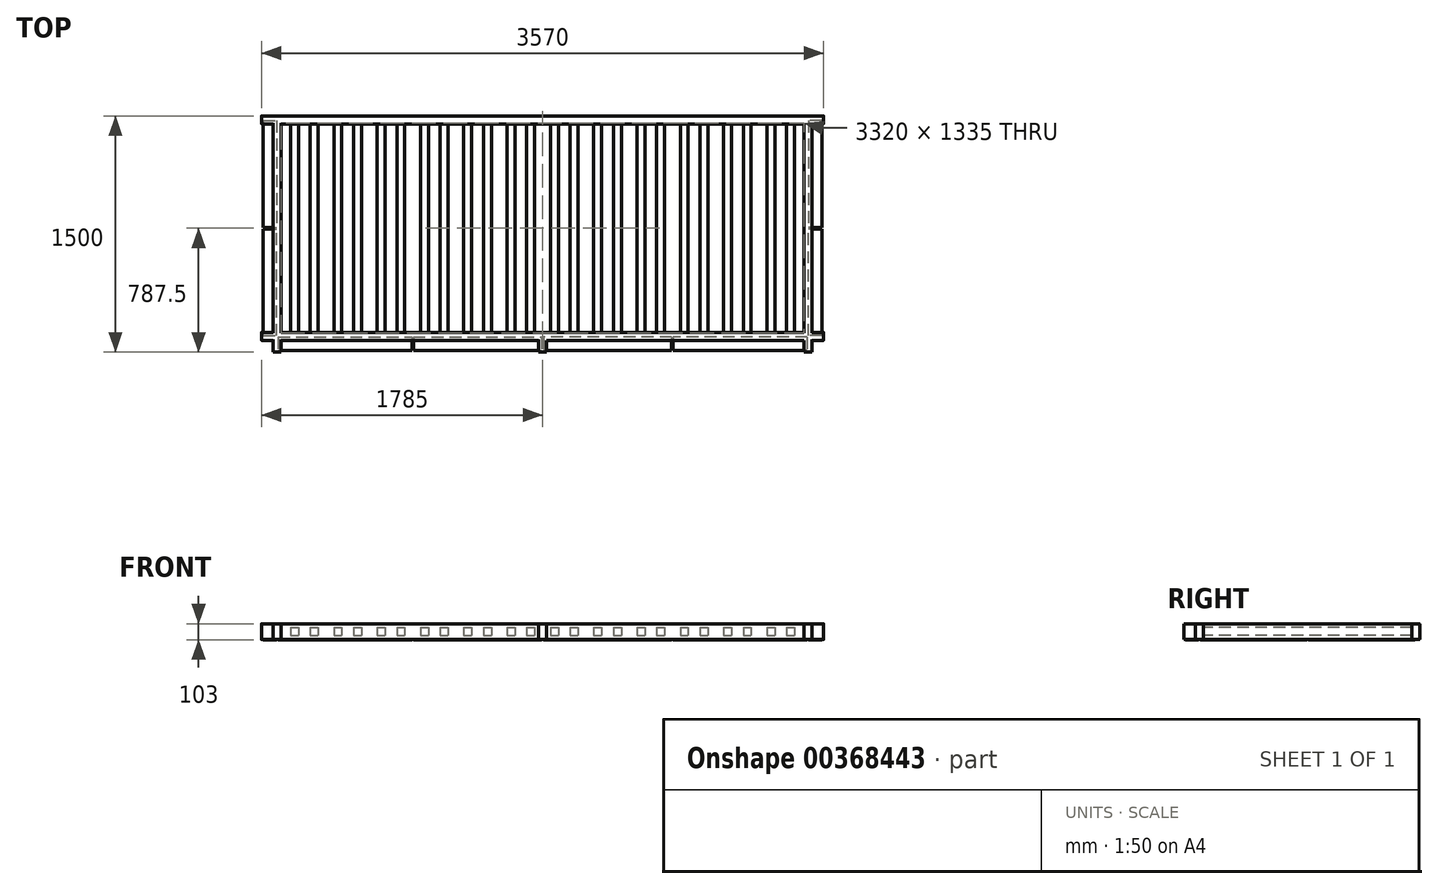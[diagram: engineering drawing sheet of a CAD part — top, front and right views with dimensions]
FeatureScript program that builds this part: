
annotation { "Feature Type Name" : "Feature", "Feature Type Description" : "" }
export const myFeature = defineFeature(function(context is Context, id is Id, definition is map)
    precondition{}
    {
        {
            var Q0;
            Q0=qCreatedBy(makeId("Top.planeOp"),FACE);
            var sketch = newSketch(context, id + "F0", { "sketchPlane" : qUnion([Q0])});
            skLineSegment(sketch, "E0.bottom", {"start": v(0, 0) * mm, "end": v(3570, 0) * mm, "construction": true});
            skLineSegment(sketch, "E0.top", {"start": v(0, 1500) * mm, "end": v(3570, 1500) * mm, "construction": true});
            skLineSegment(sketch, "E0.left", {"start": v(0, 0) * mm, "end": v(0, 1500) * mm, "construction": true});
            skLineSegment(sketch, "E0.right", {"start": v(3570, 0) * mm, "end": v(3570, 1500) * mm, "construction": true});
            skLineSegment(sketch, "E1.bottom", {"start": v(0, 1500) * mm, "end": v(3570, 1500) * mm});
            skLineSegment(sketch, "E1.top", {"start": v(0, 1450) * mm, "end": v(3570, 1450) * mm});
            skLineSegment(sketch, "E1.left", {"start": v(0, 1500) * mm, "end": v(0, 1450) * mm});
            skLineSegment(sketch, "E1.right", {"start": v(3570, 1500) * mm, "end": v(3570, 1450) * mm});
            skLineSegment(sketch, "E2.bottom", {"start": v(0, 125) * mm, "end": v(3570, 125) * mm});
            skLineSegment(sketch, "E2.top", {"start": v(0, 75) * mm, "end": v(3570, 75) * mm});
            skLineSegment(sketch, "E2.left", {"start": v(0, 125) * mm, "end": v(0, 75) * mm});
            skLineSegment(sketch, "E2.right", {"start": v(3570, 125) * mm, "end": v(3570, 75) * mm});
            skLineSegment(sketch, "E3.bottom", {"start": v(75, 1500) * mm, "end": v(125, 1500) * mm});
            skLineSegment(sketch, "E3.top", {"start": v(75, 0) * mm, "end": v(125, 0) * mm});
            skLineSegment(sketch, "E3.left", {"start": v(75, 1500) * mm, "end": v(75, 0) * mm});
            skLineSegment(sketch, "E3.right", {"start": v(125, 1500) * mm, "end": v(125, 0) * mm});
            skLineSegment(sketch, "E4.bottom", {"start": v(3445, 1500) * mm, "end": v(3495, 1500) * mm});
            skLineSegment(sketch, "E4.top", {"start": v(3445, 0) * mm, "end": v(3495, 0) * mm});
            skLineSegment(sketch, "E4.left", {"start": v(3445, 1500) * mm, "end": v(3445, 0) * mm});
            skLineSegment(sketch, "E4.right", {"start": v(3495, 1500) * mm, "end": v(3495, 0) * mm});
            skLineSegment(sketch, "E5.bottom", {"start": v(1810, 0) * mm, "end": v(1760, 0) * mm});
            skLineSegment(sketch, "E5.left", {"start": v(1810, 0) * mm, "end": v(1810, 75) * mm});
            skLineSegment(sketch, "E5.right", {"start": v(1760, 0) * mm, "end": v(1760, 75) * mm});
            skLineSegment(sketch, "E6", {"start": v(3495, 1450) * mm, "end": v(3495, 125) * mm, "construction": true});
            skLineSegment(sketch, "E7", {"start": v(75, 1450) * mm, "end": v(75, 125) * mm, "construction": true});
            skSolve(sketch);
        }
        {
            var Q0;
            Q0=qSketchRegion(id+"F0",true);
            extrude(context, id + "F1", {"entities" : qUnion([Q0]), "depth" : 75 * mm, "hasSecondDirection" : true, "secondDirectionOppositeDirection" : true, "secondDirectionDepth" : 25 * mm});
        }
        {
            var Q0;
            {var subQ0=sQuery(id+"F0.wireOp",EDGE,"E1.top");Q0=makeQuery(id+"F1.opExtrude","CAP_EDGE",EDGE,{"disambiguationData":[OSD([subQ0]),TDD([makeQuery(id+"F0.imprint","IMPRINT",EDGE,{"disambiguationData":[TD([[makeQuery(id+"F0.imprint","INTERSECT",VERTEX,{"derivedFrom":[subQ0,sQuery(id+"F0.wireOp",EDGE,"E3.right")]}),-1.0]])],"derivedFrom":subQ0})])],"isStart":false});}
            var Q1;
            Q1=makeQuery(id+"F1.opExtrude","CAP_EDGE",EDGE,{"disambiguationData":[OSD([sQuery(id+"F0.wireOp",EDGE,"E1.bottom"),sQuery(id+"F0.wireOp",EDGE,"E3.bottom"),sQuery(id+"F0.wireOp",EDGE,"E4.bottom")])],"isStart":false});
            var Q2;
            {var subQ0=sQuery(id+"F0.wireOp",EDGE,"E2.bottom");Q2=makeQuery(id+"F1.opExtrude","CAP_EDGE",EDGE,{"disambiguationData":[OSD([subQ0]),TDD([makeQuery(id+"F0.imprint","IMPRINT",EDGE,{"disambiguationData":[TD([[makeQuery(id+"F0.imprint","INTERSECT",VERTEX,{"derivedFrom":[subQ0,sQuery(id+"F0.wireOp",EDGE,"E3.right")]}),-1.0]])],"derivedFrom":subQ0})])],"isStart":false});}
            var Q3;
            {var subQ0=sQuery(id+"F0.wireOp",EDGE,"E2.top");Q3=makeQuery(id+"F1.opExtrude","CAP_EDGE",EDGE,{"disambiguationData":[OSD([subQ0]),TDD([makeQuery(id+"F0.imprint","IMPRINT",EDGE,{"disambiguationData":[TD([[makeQuery(id+"F0.imprint","INTERSECT",VERTEX,{"derivedFrom":[subQ0,sQuery(id+"F0.wireOp",EDGE,"E3.right")]}),-1.0]])],"derivedFrom":subQ0})])],"isStart":false});}
            var Q4;
            {var subQ0=sQuery(id+"F0.wireOp",EDGE,"E2.top");Q4=makeQuery(id+"F1.opExtrude","CAP_EDGE",EDGE,{"disambiguationData":[OSD([subQ0]),TDD([makeQuery(id+"F0.imprint","IMPRINT",EDGE,{"disambiguationData":[TD([[makeQuery(id+"F0.imprint","INTERSECT",VERTEX,{"derivedFrom":[subQ0,sQuery(id+"F0.wireOp",EDGE,"E2.left")]}),-1.0]])],"derivedFrom":subQ0})])],"isStart":false});}
            var Q5;
            {var subQ0=sQuery(id+"F0.wireOp",EDGE,"E2.bottom");Q5=makeQuery(id+"F1.opExtrude","CAP_EDGE",EDGE,{"disambiguationData":[OSD([subQ0]),TDD([makeQuery(id+"F0.imprint","IMPRINT",EDGE,{"disambiguationData":[TD([[makeQuery(id+"F0.imprint","INTERSECT",VERTEX,{"derivedFrom":[subQ0,sQuery(id+"F0.wireOp",EDGE,"E2.left")]}),-1.0]])],"derivedFrom":subQ0})])],"isStart":false});}
            var Q6;
            {var subQ0=sQuery(id+"F0.wireOp",EDGE,"E2.bottom");Q6=makeQuery(id+"F1.opExtrude","CAP_EDGE",EDGE,{"disambiguationData":[OSD([subQ0]),TDD([makeQuery(id+"F0.imprint","IMPRINT",EDGE,{"disambiguationData":[TD([[makeQuery(id+"F0.imprint","INTERSECT",VERTEX,{"derivedFrom":[subQ0,sQuery(id+"F0.wireOp",EDGE,"E2.right")]}),1.0]])],"derivedFrom":subQ0})])],"isStart":false});}
            var Q7;
            {var subQ0=sQuery(id+"F0.wireOp",EDGE,"E2.top");Q7=makeQuery(id+"F1.opExtrude","CAP_EDGE",EDGE,{"disambiguationData":[OSD([subQ0]),TDD([makeQuery(id+"F0.imprint","IMPRINT",EDGE,{"disambiguationData":[TD([[makeQuery(id+"F0.imprint","INTERSECT",VERTEX,{"derivedFrom":[subQ0,sQuery(id+"F0.wireOp",EDGE,"E2.right")]}),1.0]])],"derivedFrom":subQ0})])],"isStart":false});}
            var Q8;
            {var subQ0=sQuery(id+"F0.wireOp",EDGE,"E1.top");Q8=makeQuery(id+"F1.opExtrude","CAP_EDGE",EDGE,{"disambiguationData":[OSD([subQ0]),TDD([makeQuery(id+"F0.imprint","IMPRINT",EDGE,{"disambiguationData":[TD([[makeQuery(id+"F0.imprint","INTERSECT",VERTEX,{"derivedFrom":[subQ0,sQuery(id+"F0.wireOp",EDGE,"E1.right")]}),1.0]])],"derivedFrom":subQ0})])],"isStart":false});}
            var Q9;
            {var subQ0=sQuery(id+"F0.wireOp",EDGE,"E1.top");Q9=makeQuery(id+"F1.opExtrude","CAP_EDGE",EDGE,{"disambiguationData":[OSD([subQ0]),TDD([makeQuery(id+"F0.imprint","IMPRINT",EDGE,{"disambiguationData":[TD([[makeQuery(id+"F0.imprint","INTERSECT",VERTEX,{"derivedFrom":[subQ0,sQuery(id+"F0.wireOp",EDGE,"E1.left")]}),-1.0]])],"derivedFrom":subQ0})])],"isStart":false});}
            var Q10;
            Q10=makeQuery(id+"F1.opExtrude","CAP_EDGE",EDGE,{"disambiguationData":[OSD([sQuery(id+"F0.wireOp",EDGE,"E1.bottom"),sQuery(id+"F0.wireOp",EDGE,"E3.bottom"),sQuery(id+"F0.wireOp",EDGE,"E4.bottom")])],"isStart":true});
            var Q11;
            {var subQ0=sQuery(id+"F0.wireOp",EDGE,"E1.top");Q11=makeQuery(id+"F1.opExtrude","CAP_EDGE",EDGE,{"disambiguationData":[OSD([subQ0]),TDD([makeQuery(id+"F0.imprint","IMPRINT",EDGE,{"disambiguationData":[TD([[makeQuery(id+"F0.imprint","INTERSECT",VERTEX,{"derivedFrom":[subQ0,sQuery(id+"F0.wireOp",EDGE,"E3.right")]}),-1.0]])],"derivedFrom":subQ0})])],"isStart":true});}
            var Q12;
            {var subQ0=sQuery(id+"F0.wireOp",EDGE,"E1.top");Q12=makeQuery(id+"F1.opExtrude","CAP_EDGE",EDGE,{"disambiguationData":[OSD([subQ0]),TDD([makeQuery(id+"F0.imprint","IMPRINT",EDGE,{"disambiguationData":[TD([[makeQuery(id+"F0.imprint","INTERSECT",VERTEX,{"derivedFrom":[subQ0,sQuery(id+"F0.wireOp",EDGE,"E1.right")]}),1.0]])],"derivedFrom":subQ0})])],"isStart":true});}
            var Q13;
            {var subQ0=sQuery(id+"F0.wireOp",EDGE,"E2.top");Q13=makeQuery(id+"F1.opExtrude","CAP_EDGE",EDGE,{"disambiguationData":[OSD([subQ0]),TDD([makeQuery(id+"F0.imprint","IMPRINT",EDGE,{"disambiguationData":[TD([[makeQuery(id+"F0.imprint","INTERSECT",VERTEX,{"derivedFrom":[subQ0,sQuery(id+"F0.wireOp",EDGE,"E2.right")]}),1.0]])],"derivedFrom":subQ0})])],"isStart":true});}
            var Q14;
            {var subQ0=sQuery(id+"F0.wireOp",EDGE,"E2.bottom");Q14=makeQuery(id+"F1.opExtrude","CAP_EDGE",EDGE,{"disambiguationData":[OSD([subQ0]),TDD([makeQuery(id+"F0.imprint","IMPRINT",EDGE,{"disambiguationData":[TD([[makeQuery(id+"F0.imprint","INTERSECT",VERTEX,{"derivedFrom":[subQ0,sQuery(id+"F0.wireOp",EDGE,"E2.right")]}),1.0]])],"derivedFrom":subQ0})])],"isStart":true});}
            var Q15;
            {var subQ0=sQuery(id+"F0.wireOp",EDGE,"E2.bottom");Q15=makeQuery(id+"F1.opExtrude","CAP_EDGE",EDGE,{"disambiguationData":[OSD([subQ0]),TDD([makeQuery(id+"F0.imprint","IMPRINT",EDGE,{"disambiguationData":[TD([[makeQuery(id+"F0.imprint","INTERSECT",VERTEX,{"derivedFrom":[subQ0,sQuery(id+"F0.wireOp",EDGE,"E3.right")]}),-1.0]])],"derivedFrom":subQ0})])],"isStart":true});}
            var Q16;
            {var subQ0=sQuery(id+"F0.wireOp",EDGE,"E2.top");Q16=makeQuery(id+"F1.opExtrude","CAP_EDGE",EDGE,{"disambiguationData":[OSD([subQ0]),TDD([makeQuery(id+"F0.imprint","IMPRINT",EDGE,{"disambiguationData":[TD([[makeQuery(id+"F0.imprint","INTERSECT",VERTEX,{"derivedFrom":[subQ0,sQuery(id+"F0.wireOp",EDGE,"E3.right")]}),-1.0]])],"derivedFrom":subQ0})])],"isStart":true});}
            var Q17;
            {var subQ0=sQuery(id+"F0.wireOp",EDGE,"E2.bottom");Q17=makeQuery(id+"F1.opExtrude","CAP_EDGE",EDGE,{"disambiguationData":[OSD([subQ0]),TDD([makeQuery(id+"F0.imprint","IMPRINT",EDGE,{"disambiguationData":[TD([[makeQuery(id+"F0.imprint","INTERSECT",VERTEX,{"derivedFrom":[subQ0,sQuery(id+"F0.wireOp",EDGE,"E2.left")]}),-1.0]])],"derivedFrom":subQ0})])],"isStart":true});}
            var Q18;
            {var subQ0=sQuery(id+"F0.wireOp",EDGE,"E2.top");Q18=makeQuery(id+"F1.opExtrude","CAP_EDGE",EDGE,{"disambiguationData":[OSD([subQ0]),TDD([makeQuery(id+"F0.imprint","IMPRINT",EDGE,{"disambiguationData":[TD([[makeQuery(id+"F0.imprint","INTERSECT",VERTEX,{"derivedFrom":[subQ0,sQuery(id+"F0.wireOp",EDGE,"E2.left")]}),-1.0]])],"derivedFrom":subQ0})])],"isStart":true});}
            var Q19;
            {var subQ0=sQuery(id+"F0.wireOp",EDGE,"E1.top");Q19=makeQuery(id+"F1.opExtrude","CAP_EDGE",EDGE,{"disambiguationData":[OSD([subQ0]),TDD([makeQuery(id+"F0.imprint","IMPRINT",EDGE,{"disambiguationData":[TD([[makeQuery(id+"F0.imprint","INTERSECT",VERTEX,{"derivedFrom":[subQ0,sQuery(id+"F0.wireOp",EDGE,"E1.left")]}),-1.0]])],"derivedFrom":subQ0})])],"isStart":true});}
            fillet(context, id + "F2", {"entities" : qUnion([Q0, Q1, Q2, Q3, Q4, Q5, Q6, Q7, Q8, Q9, Q10, Q11, Q12, Q13, Q14, Q15, Q16, Q17, Q18, Q19]), "radius" : 5 * mm, "tangentPropagation" : true, "allowEdgeOverflow" : false});
        }
        {
            var Q0;
            Q0=qCreatedBy(makeId("Top.planeOp"),FACE);
            var sketch = newSketch(context, id + "F3", { "sketchPlane" : qUnion([Q0])});
            skLineSegment(sketch, "E8.bottom", {"start": v(185, 1450) * mm, "end": v(235, 1450) * mm});
            skLineSegment(sketch, "E8.top", {"start": v(185, 125) * mm, "end": v(235, 125) * mm});
            skLineSegment(sketch, "E8.left", {"start": v(185, 1450) * mm, "end": v(185, 125) * mm});
            skLineSegment(sketch, "E8.right", {"start": v(235, 1450) * mm, "end": v(235, 125) * mm});
            skLineSegment(sketch, "E9.bottom", {"start": v(310, 1450) * mm, "end": v(360, 1450) * mm});
            skLineSegment(sketch, "E9.top", {"start": v(310, 125) * mm, "end": v(360, 125) * mm});
            skLineSegment(sketch, "E9.left", {"start": v(310, 1450) * mm, "end": v(310, 125) * mm});
            skLineSegment(sketch, "E9.right", {"start": v(360, 1450) * mm, "end": v(360, 125) * mm});
            skLineSegment(sketch, "E10", {"start": v(235, 125) * mm, "end": v(387, 125) * mm, "construction": true});
            skLineSegment(sketch, "E11", {"start": v(235, 1450) * mm, "end": v(386.34, 1450) * mm, "construction": true});
            skLineSegment(sketch, "E12.1.0.0", {"start": v(635, 1450) * mm, "end": v(635, 125) * mm});
            skLineSegment(sketch, "E12.1.0.1", {"start": v(585, 1450) * mm, "end": v(585, 125) * mm});
            skLineSegment(sketch, "E12.1.0.2", {"start": v(510, 1450) * mm, "end": v(510, 125) * mm});
            skLineSegment(sketch, "E12.1.0.3", {"start": v(460, 1450) * mm, "end": v(460, 125) * mm});
            skLineSegment(sketch, "E12.1.0.4", {"start": v(460, 125) * mm, "end": v(510, 125) * mm});
            skLineSegment(sketch, "E12.1.0.5", {"start": v(460, 1450) * mm, "end": v(510, 1450) * mm});
            skLineSegment(sketch, "E12.1.0.6", {"start": v(585, 125) * mm, "end": v(635, 125) * mm});
            skLineSegment(sketch, "E12.1.0.7", {"start": v(585, 1450) * mm, "end": v(635, 1450) * mm});
            skLineSegment(sketch, "E12.2.0.0", {"start": v(910, 1450) * mm, "end": v(910, 125) * mm});
            skLineSegment(sketch, "E12.2.0.1", {"start": v(860, 1450) * mm, "end": v(860, 125) * mm});
            skLineSegment(sketch, "E12.2.0.2", {"start": v(785, 1450) * mm, "end": v(785, 125) * mm});
            skLineSegment(sketch, "E12.2.0.3", {"start": v(735, 1450) * mm, "end": v(735, 125) * mm});
            skLineSegment(sketch, "E12.2.0.4", {"start": v(735, 125) * mm, "end": v(785, 125) * mm});
            skLineSegment(sketch, "E12.2.0.5", {"start": v(735, 1450) * mm, "end": v(785, 1450) * mm});
            skLineSegment(sketch, "E12.2.0.6", {"start": v(860, 125) * mm, "end": v(910, 125) * mm});
            skLineSegment(sketch, "E12.2.0.7", {"start": v(860, 1450) * mm, "end": v(910, 1450) * mm});
            skLineSegment(sketch, "E12.3.0.0", {"start": v(1185, 1450) * mm, "end": v(1185, 125) * mm});
            skLineSegment(sketch, "E12.3.0.1", {"start": v(1135, 1450) * mm, "end": v(1135, 125) * mm});
            skLineSegment(sketch, "E12.3.0.2", {"start": v(1060, 1450) * mm, "end": v(1060, 125) * mm});
            skLineSegment(sketch, "E12.3.0.3", {"start": v(1010, 1450) * mm, "end": v(1010, 125) * mm});
            skLineSegment(sketch, "E12.3.0.4", {"start": v(1010, 125) * mm, "end": v(1060, 125) * mm});
            skLineSegment(sketch, "E12.3.0.5", {"start": v(1010, 1450) * mm, "end": v(1060, 1450) * mm});
            skLineSegment(sketch, "E12.3.0.6", {"start": v(1135, 125) * mm, "end": v(1185, 125) * mm});
            skLineSegment(sketch, "E12.3.0.7", {"start": v(1135, 1450) * mm, "end": v(1185, 1450) * mm});
            skLineSegment(sketch, "E12.4.0.0", {"start": v(1460, 1450) * mm, "end": v(1460, 125) * mm});
            skLineSegment(sketch, "E12.4.0.1", {"start": v(1410, 1450) * mm, "end": v(1410, 125) * mm});
            skLineSegment(sketch, "E12.4.0.2", {"start": v(1335, 1450) * mm, "end": v(1335, 125) * mm});
            skLineSegment(sketch, "E12.4.0.3", {"start": v(1285, 1450) * mm, "end": v(1285, 125) * mm});
            skLineSegment(sketch, "E12.4.0.4", {"start": v(1285, 125) * mm, "end": v(1335, 125) * mm});
            skLineSegment(sketch, "E12.4.0.5", {"start": v(1285, 1450) * mm, "end": v(1335, 1450) * mm});
            skLineSegment(sketch, "E12.4.0.6", {"start": v(1410, 125) * mm, "end": v(1460, 125) * mm});
            skLineSegment(sketch, "E12.4.0.7", {"start": v(1410, 1450) * mm, "end": v(1460, 1450) * mm});
            skLineSegment(sketch, "E12.5.0.0", {"start": v(1735, 1450) * mm, "end": v(1735, 125) * mm});
            skLineSegment(sketch, "E12.5.0.1", {"start": v(1685, 1450) * mm, "end": v(1685, 125) * mm});
            skLineSegment(sketch, "E12.5.0.2", {"start": v(1610, 1450) * mm, "end": v(1610, 125) * mm});
            skLineSegment(sketch, "E12.5.0.3", {"start": v(1560, 1450) * mm, "end": v(1560, 125) * mm});
            skLineSegment(sketch, "E12.5.0.4", {"start": v(1560, 125) * mm, "end": v(1610, 125) * mm});
            skLineSegment(sketch, "E12.5.0.5", {"start": v(1560, 1450) * mm, "end": v(1610, 1450) * mm});
            skLineSegment(sketch, "E12.5.0.6", {"start": v(1685, 125) * mm, "end": v(1735, 125) * mm});
            skLineSegment(sketch, "E12.5.0.7", {"start": v(1685, 1450) * mm, "end": v(1735, 1450) * mm});
            skLineSegment(sketch, "E12.6.0.0", {"start": v(2010, 1450) * mm, "end": v(2010, 125) * mm});
            skLineSegment(sketch, "E12.6.0.1", {"start": v(1960, 1450) * mm, "end": v(1960, 125) * mm});
            skLineSegment(sketch, "E12.6.0.2", {"start": v(1885, 1450) * mm, "end": v(1885, 125) * mm});
            skLineSegment(sketch, "E12.6.0.3", {"start": v(1835, 1450) * mm, "end": v(1835, 125) * mm});
            skLineSegment(sketch, "E12.6.0.4", {"start": v(1835, 125) * mm, "end": v(1885, 125) * mm});
            skLineSegment(sketch, "E12.6.0.5", {"start": v(1835, 1450) * mm, "end": v(1885, 1450) * mm});
            skLineSegment(sketch, "E12.6.0.6", {"start": v(1960, 125) * mm, "end": v(2010, 125) * mm});
            skLineSegment(sketch, "E12.6.0.7", {"start": v(1960, 1450) * mm, "end": v(2010, 1450) * mm});
            skLineSegment(sketch, "E12.7.0.0", {"start": v(2285, 1450) * mm, "end": v(2285, 125) * mm});
            skLineSegment(sketch, "E12.7.0.1", {"start": v(2235, 1450) * mm, "end": v(2235, 125) * mm});
            skLineSegment(sketch, "E12.7.0.2", {"start": v(2160, 1450) * mm, "end": v(2160, 125) * mm});
            skLineSegment(sketch, "E12.7.0.3", {"start": v(2110, 1450) * mm, "end": v(2110, 125) * mm});
            skLineSegment(sketch, "E12.7.0.4", {"start": v(2110, 125) * mm, "end": v(2160, 125) * mm});
            skLineSegment(sketch, "E12.7.0.5", {"start": v(2110, 1450) * mm, "end": v(2160, 1450) * mm});
            skLineSegment(sketch, "E12.7.0.6", {"start": v(2235, 125) * mm, "end": v(2285, 125) * mm});
            skLineSegment(sketch, "E12.7.0.7", {"start": v(2235, 1450) * mm, "end": v(2285, 1450) * mm});
            skLineSegment(sketch, "E12.8.0.0", {"start": v(2560, 1450) * mm, "end": v(2560, 125) * mm});
            skLineSegment(sketch, "E12.8.0.1", {"start": v(2510, 1450) * mm, "end": v(2510, 125) * mm});
            skLineSegment(sketch, "E12.8.0.2", {"start": v(2435, 1450) * mm, "end": v(2435, 125) * mm});
            skLineSegment(sketch, "E12.8.0.3", {"start": v(2385, 1450) * mm, "end": v(2385, 125) * mm});
            skLineSegment(sketch, "E12.8.0.4", {"start": v(2385, 125) * mm, "end": v(2435, 125) * mm});
            skLineSegment(sketch, "E12.8.0.5", {"start": v(2385, 1450) * mm, "end": v(2435, 1450) * mm});
            skLineSegment(sketch, "E12.8.0.6", {"start": v(2510, 125) * mm, "end": v(2560, 125) * mm});
            skLineSegment(sketch, "E12.8.0.7", {"start": v(2510, 1450) * mm, "end": v(2560, 1450) * mm});
            skLineSegment(sketch, "E12.9.0.0", {"start": v(2835, 1450) * mm, "end": v(2835, 125) * mm});
            skLineSegment(sketch, "E12.9.0.1", {"start": v(2785, 1450) * mm, "end": v(2785, 125) * mm});
            skLineSegment(sketch, "E12.9.0.2", {"start": v(2710, 1450) * mm, "end": v(2710, 125) * mm});
            skLineSegment(sketch, "E12.9.0.3", {"start": v(2660, 1450) * mm, "end": v(2660, 125) * mm});
            skLineSegment(sketch, "E12.9.0.4", {"start": v(2660, 125) * mm, "end": v(2710, 125) * mm});
            skLineSegment(sketch, "E12.9.0.5", {"start": v(2660, 1450) * mm, "end": v(2710, 1450) * mm});
            skLineSegment(sketch, "E12.9.0.6", {"start": v(2785, 125) * mm, "end": v(2835, 125) * mm});
            skLineSegment(sketch, "E12.9.0.7", {"start": v(2785, 1450) * mm, "end": v(2835, 1450) * mm});
            skLineSegment(sketch, "E12.10.0.0", {"start": v(3110, 1450) * mm, "end": v(3110, 125) * mm});
            skLineSegment(sketch, "E12.10.0.1", {"start": v(3060, 1450) * mm, "end": v(3060, 125) * mm});
            skLineSegment(sketch, "E12.10.0.2", {"start": v(2985, 1450) * mm, "end": v(2985, 125) * mm});
            skLineSegment(sketch, "E12.10.0.3", {"start": v(2935, 1450) * mm, "end": v(2935, 125) * mm});
            skLineSegment(sketch, "E12.10.0.4", {"start": v(2935, 125) * mm, "end": v(2985, 125) * mm});
            skLineSegment(sketch, "E12.10.0.5", {"start": v(2935, 1450) * mm, "end": v(2985, 1450) * mm});
            skLineSegment(sketch, "E12.10.0.6", {"start": v(3060, 125) * mm, "end": v(3110, 125) * mm});
            skLineSegment(sketch, "E12.10.0.7", {"start": v(3060, 1450) * mm, "end": v(3110, 1450) * mm});
            skLineSegment(sketch, "E12.11.0.0", {"start": v(3385, 1450) * mm, "end": v(3385, 125) * mm});
            skLineSegment(sketch, "E12.11.0.1", {"start": v(3335, 1450) * mm, "end": v(3335, 125) * mm});
            skLineSegment(sketch, "E12.11.0.2", {"start": v(3260, 1450) * mm, "end": v(3260, 125) * mm});
            skLineSegment(sketch, "E12.11.0.3", {"start": v(3210, 1450) * mm, "end": v(3210, 125) * mm});
            skLineSegment(sketch, "E12.11.0.4", {"start": v(3210, 125) * mm, "end": v(3260, 125) * mm});
            skLineSegment(sketch, "E12.11.0.5", {"start": v(3210, 1450) * mm, "end": v(3260, 1450) * mm});
            skLineSegment(sketch, "E12.11.0.6", {"start": v(3335, 125) * mm, "end": v(3385, 125) * mm});
            skLineSegment(sketch, "E12.11.0.7", {"start": v(3335, 1450) * mm, "end": v(3385, 1450) * mm});
            skLineSegment(sketch, "E12.direction1", {"start": v(185, 125) * mm, "end": v(460, 125) * mm, "construction": true});
            skSolve(sketch);
        }
        {
            var Q0;
            Q0=qSketchRegion(id+"F3",true);
            extrude(context, id + "F4", {"entities" : qUnion([Q0]), "depth" : 50 * mm});
        }
        {
            var Q0;
            Q0=makeQuery(id+"F1.opExtrude","CAP_FACE",FACE,{"disambiguationData":[OSD([sQuery(id+"F0.wireOp",EDGE,"E1.bottom"),sQuery(id+"F0.wireOp",EDGE,"E1.top"),sQuery(id+"F0.wireOp",EDGE,"E1.left"),sQuery(id+"F0.wireOp",EDGE,"E1.right"),sQuery(id+"F0.wireOp",EDGE,"E2.bottom"),sQuery(id+"F0.wireOp",EDGE,"E2.top"),sQuery(id+"F0.wireOp",EDGE,"E2.left"),sQuery(id+"F0.wireOp",EDGE,"E2.right"),sQuery(id+"F0.wireOp",EDGE,"E3.bottom"),sQuery(id+"F0.wireOp",EDGE,"E3.top"),sQuery(id+"F0.wireOp",EDGE,"E3.left"),sQuery(id+"F0.wireOp",EDGE,"E3.right"),sQuery(id+"F0.wireOp",EDGE,"E4.bottom"),sQuery(id+"F0.wireOp",EDGE,"E4.top"),sQuery(id+"F0.wireOp",EDGE,"E4.left"),sQuery(id+"F0.wireOp",EDGE,"E4.right"),sQuery(id+"F0.wireOp",EDGE,"E5.bottom"),sQuery(id+"F0.wireOp",EDGE,"E5.left"),sQuery(id+"F0.wireOp",EDGE,"E5.right"),sQuery(id+"F0.wireOp",EDGE,"nKdBA3m5-DK9h-MpKn-nGnI-esfd6mOMu1i7.bottom"),sQuery(id+"F0.wireOp",EDGE,"nKdBA3m5-DK9h-MpKn-nGnI-esfd6mOMu1i7.top"),sQuery(id+"F0.wireOp",EDGE,"nKdBA3m5-DK9h-MpKn-nGnI-esfd6mOMu1i7.left"),sQuery(id+"F0.wireOp",EDGE,"ZkKdbLk1-IUnF-EuSR-hseP-fomAbPEtOkAG.bottom"),sQuery(id+"F0.wireOp",EDGE,"ZkKdbLk1-IUnF-EuSR-hseP-fomAbPEtOkAG.top"),sQuery(id+"F0.wireOp",EDGE,"ZkKdbLk1-IUnF-EuSR-hseP-fomAbPEtOkAG.left")])],"isStart":true});
            var sketch = newSketch(context, id + "F5", { "sketchPlane" : qUnion([Q0])});
            skLineSegment(sketch, "E13.bottom", {"start": v(3560, -1470) * mm, "end": v(3475, -1470) * mm});
            skLineSegment(sketch, "E13.top", {"start": v(3560, -792.5) * mm, "end": v(3475, -792.5) * mm});
            skLineSegment(sketch, "E13.left", {"start": v(3560, -1470) * mm, "end": v(3560, -792.5) * mm});
            skLineSegment(sketch, "E13.right", {"start": v(3475, -1470) * mm, "end": v(3475, -792.5) * mm});
            skLineSegment(sketch, "E14", {"start": v(3445, -787.5) * mm, "end": v(3710.6, -787.5) * mm, "construction": true});
            skLineSegment(sketch, "E15.MirrorCS", {"start": v(3560, -105) * mm, "end": v(3475, -105) * mm});
            skLineSegment(sketch, "E16.MirrorCS", {"start": v(3475, -105) * mm, "end": v(3475, -782.5) * mm});
            skLineSegment(sketch, "E17.MirrorCS", {"start": v(3560, -105) * mm, "end": v(3560, -782.5) * mm});
            skLineSegment(sketch, "E18.MirrorCS", {"start": v(3560, -782.5) * mm, "end": v(3475, -782.5) * mm});
            skLineSegment(sketch, "E19", {"start": v(1785, 0) * mm, "end": v(1785, -316.49) * mm, "construction": true});
            skPoint(sketch, "E19.endSnap0", {"position": v(1785, 0) * mm});
            skLineSegment(sketch, "E20.MirrorCS", {"start": v(10, -1470) * mm, "end": v(95, -1470) * mm});
            skLineSegment(sketch, "E21.MirrorCS", {"start": v(10, -105) * mm, "end": v(95, -105) * mm});
            skLineSegment(sketch, "E22.MirrorCS", {"start": v(10, -1470) * mm, "end": v(10, -792.5) * mm});
            skLineSegment(sketch, "E23.MirrorCS", {"start": v(95, -105) * mm, "end": v(95, -782.5) * mm});
            skLineSegment(sketch, "E24.MirrorCS", {"start": v(95, -1470) * mm, "end": v(95, -792.5) * mm});
            skLineSegment(sketch, "E25.MirrorCS", {"start": v(10, -792.5) * mm, "end": v(95, -792.5) * mm});
            skLineSegment(sketch, "E26.MirrorCS", {"start": v(10, -782.5) * mm, "end": v(95, -782.5) * mm});
            skLineSegment(sketch, "E27.MirrorCS", {"start": v(10, -105) * mm, "end": v(10, -782.5) * mm});
            skLineSegment(sketch, "E28.bottom", {"start": v(3465, -95) * mm, "end": v(2615, -95) * mm});
            skLineSegment(sketch, "E28.top", {"start": v(3465, -10) * mm, "end": v(2615, -10) * mm});
            skLineSegment(sketch, "E28.left", {"start": v(3465, -95) * mm, "end": v(3465, -10) * mm});
            skLineSegment(sketch, "E28.right", {"start": v(2615, -95) * mm, "end": v(2615, -10) * mm});
            skLineSegment(sketch, "E29.bottom", {"start": v(2605, -95) * mm, "end": v(1790, -95) * mm});
            skLineSegment(sketch, "E29.top", {"start": v(2605, -10) * mm, "end": v(1790, -10) * mm});
            skLineSegment(sketch, "E29.left", {"start": v(2605, -95) * mm, "end": v(2605, -10) * mm});
            skLineSegment(sketch, "E29.right", {"start": v(1790, -95) * mm, "end": v(1790, -10) * mm});
            skLineSegment(sketch, "E30.MirrorCS", {"start": v(105, -10) * mm, "end": v(955, -10) * mm});
            skLineSegment(sketch, "E31.MirrorCS", {"start": v(105, -95) * mm, "end": v(105, -10) * mm});
            skLineSegment(sketch, "E32.MirrorCS", {"start": v(965, -95) * mm, "end": v(965, -10) * mm});
            skLineSegment(sketch, "E33.MirrorCS", {"start": v(105, -95) * mm, "end": v(955, -95) * mm});
            skLineSegment(sketch, "E34.MirrorCS", {"start": v(955, -95) * mm, "end": v(955, -10) * mm});
            skLineSegment(sketch, "E35.MirrorCS", {"start": v(1780, -95) * mm, "end": v(1780, -10) * mm});
            skLineSegment(sketch, "E36.MirrorCS", {"start": v(965, -10) * mm, "end": v(1780, -10) * mm});
            skLineSegment(sketch, "E37.MirrorCS", {"start": v(965, -95) * mm, "end": v(1780, -95) * mm});
            skSolve(sketch);
        }
        {
            var Q0;
            Q0=qSketchRegion(id+"F5",true);
            extrude(context, id + "F6", {"entities" : qUnion([Q0]), "operationType" : NewBodyOperationType.ADD, "depth" : 3 * mm});
        }
    });
